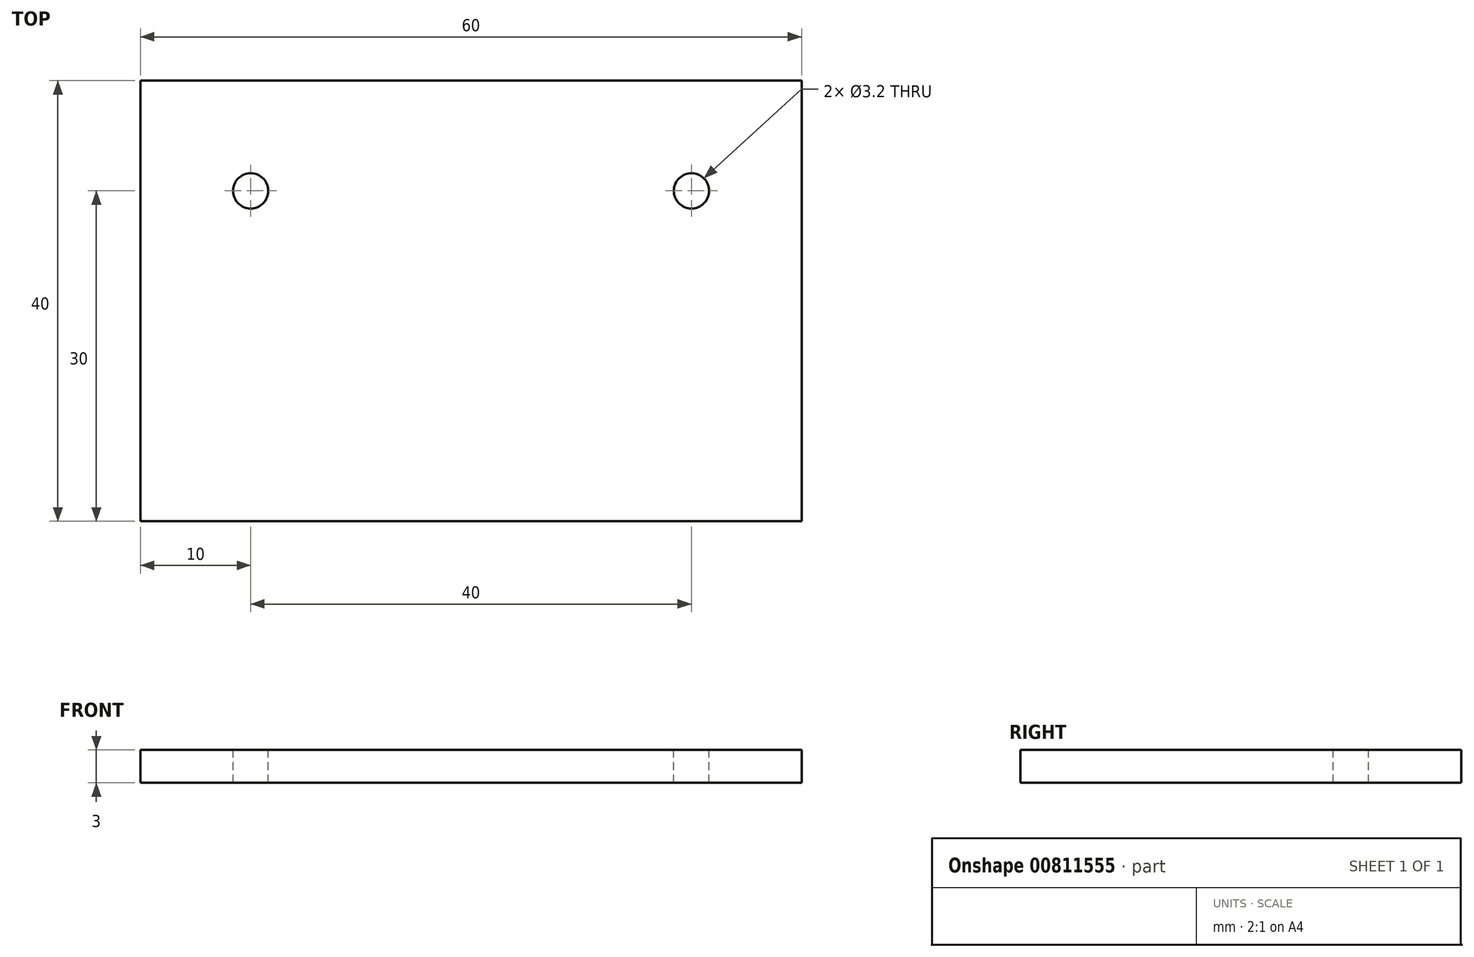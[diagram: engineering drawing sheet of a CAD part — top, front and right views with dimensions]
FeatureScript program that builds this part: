
annotation { "Feature Type Name" : "Feature", "Feature Type Description" : "" }
export const myFeature = defineFeature(function(context is Context, id is Id, definition is map)
    precondition{}
    {
        {
            var Q0;
            Q0=qCreatedBy(makeId("Top.planeOp"),FACE);
            var sketch = newSketch(context, id + "F0", { "sketchPlane" : qUnion([Q0])});
            skLineSegment(sketch, "E0.bottom", {"start": v(30, -20) * mm, "end": v(-30, -20) * mm});
            skLineSegment(sketch, "E0.top", {"start": v(30, 20) * mm, "end": v(-30, 20) * mm});
            skLineSegment(sketch, "E0.left", {"start": v(30, -20) * mm, "end": v(30, 20) * mm});
            skLineSegment(sketch, "E0.right", {"start": v(-30, -20) * mm, "end": v(-30, 20) * mm});
            skPoint(sketch, "E0.middle", {"position": v(0, 0) * mm});
            skSolve(sketch);
        }
        {
            var Q0;
            Q0=qSketchRegion(id+"F0",true);
            extrude(context, id + "F1", {"entities" : qUnion([Q0]), "depth" : 3 * mm, "offsetDistance" : 25 * mm});
        }
        {
            var Q0;
            Q0=makeQuery(id+"F1.opExtrude","CAP_FACE",FACE,{"disambiguationData":[OSD([sQuery(id+"F0.wireOp",EDGE,"E0.bottom"),sQuery(id+"F0.wireOp",EDGE,"E0.top"),sQuery(id+"F0.wireOp",EDGE,"E0.left"),sQuery(id+"F0.wireOp",EDGE,"E0.right")])],"isStart":false});
            var sketch = newSketch(context, id + "F2", { "sketchPlane" : qUnion([Q0])});
            skLineSegment(sketch, "E1", {"start": v(0, 20) * mm, "end": v(0, -20) * mm, "construction": true});
            skLineSegment(sketch, "E2", {"start": v(-30, 0) * mm, "end": v(30, 0) * mm, "construction": true});
            skPoint(sketch, "E3", {"position": v(-20, 10) * mm});
            skPoint(sketch, "E4", {"position": v(20, 10) * mm});
            skLineSegment(sketch, "E5.bottom", {"start": v(-30, 0) * mm, "end": v(30, 0) * mm});
            skLineSegment(sketch, "E5.top", {"start": v(-30, -20) * mm, "end": v(30, -20) * mm});
            skLineSegment(sketch, "E5.left", {"start": v(-30, 0) * mm, "end": v(-30, -20) * mm});
            skLineSegment(sketch, "E5.right", {"start": v(30, 0) * mm, "end": v(30, -20) * mm});
            skLineSegment(sketch, "E6", {"start": v(-30, -10) * mm, "end": v(30, -10) * mm, "construction": true});
            skLineSegment(sketch, "E7.bottom", {"start": v(-30, 0) * mm, "end": v(0, 0) * mm, "construction": true});
            skLineSegment(sketch, "E7.top", {"start": v(-30, -20) * mm, "end": v(0, -20) * mm, "construction": true});
            skLineSegment(sketch, "E7.left", {"start": v(-30, 0) * mm, "end": v(-30, -20) * mm, "construction": true});
            skLineSegment(sketch, "E7.right", {"start": v(0, 0) * mm, "end": v(0, -20) * mm, "construction": true});
            skLineSegment(sketch, "E8.bottom", {"start": v(0, 0) * mm, "end": v(30, 0) * mm, "construction": true});
            skLineSegment(sketch, "E8.top", {"start": v(0, -20) * mm, "end": v(30, -20) * mm, "construction": true});
            skLineSegment(sketch, "E8.right", {"start": v(30, 0) * mm, "end": v(30, -20) * mm, "construction": true});
            skLineSegment(sketch, "E9", {"start": v(15, 0) * mm, "end": v(15, -20) * mm, "construction": true});
            skCircle(sketch, "E10", {"center": v(-10, -10) * mm, "radius": 5 * mm});
            skCircle(sketch, "E11", {"center": v(10, -10) * mm, "radius": 5 * mm});
            skLineSegment(sketch, "E12", {"start": v(-15, 0) * mm, "end": v(-15, -20) * mm, "construction": true});
            skLineSegment(sketch, "E13.bottom", {"start": v(-30, 20) * mm, "end": v(0, 20) * mm, "construction": true});
            skLineSegment(sketch, "E13.left", {"start": v(-30, 20) * mm, "end": v(-30, 0) * mm, "construction": true});
            skLineSegment(sketch, "E13.right", {"start": v(0, 20) * mm, "end": v(0, 0) * mm, "construction": true});
            skLineSegment(sketch, "E14.bottom", {"start": v(0, 20) * mm, "end": v(30, 20) * mm, "construction": true});
            skLineSegment(sketch, "E14.right", {"start": v(30, 20) * mm, "end": v(30, 0) * mm, "construction": true});
            skLineSegment(sketch, "E15", {"start": v(-15, 0) * mm, "end": v(-15, 20) * mm, "construction": true});
            skLineSegment(sketch, "E16", {"start": v(-30, 10) * mm, "end": v(0, 10) * mm, "construction": true});
            skLineSegment(sketch, "E17", {"start": v(0, 10) * mm, "end": v(30, 10) * mm, "construction": true});
            skLineSegment(sketch, "E18", {"start": v(15, 0) * mm, "end": v(15, 20) * mm, "construction": true});
            skSolve(sketch);
        }
        {
            var Q0;
            Q0=sQuery(id+"F2.wireOp",VERTEX,"E3");
            var Q1;
            Q1=sQuery(id+"F2.wireOp",VERTEX,"E4");
            var Q2;
            Q2=makeQuery(id+"F1.opExtrude","SWEPT_BODY",BODY,{"disambiguationData":[OSD([sQuery(id+"F0.wireOp",EDGE,"E0.bottom"),sQuery(id+"F0.wireOp",EDGE,"E0.top"),sQuery(id+"F0.wireOp",EDGE,"E0.left"),sQuery(id+"F0.wireOp",EDGE,"E0.right")])]});
            hole(context, id + "F3", {"style" : HoleStyle.SIMPLE, "endStyle" : HoleEndStyle.BLIND, "holeDiameter" : 3.2 * mm, "majorDiameter" : 5 * mm, "holeDepth" : 5 * mm, "isTappedThrough" : true, "tappedDepth" : 12 * mm, "tapClearance" : 3, "locations" : qUnion([Q0, Q1]), "scope" : qUnion([Q2])});
        }
    });
